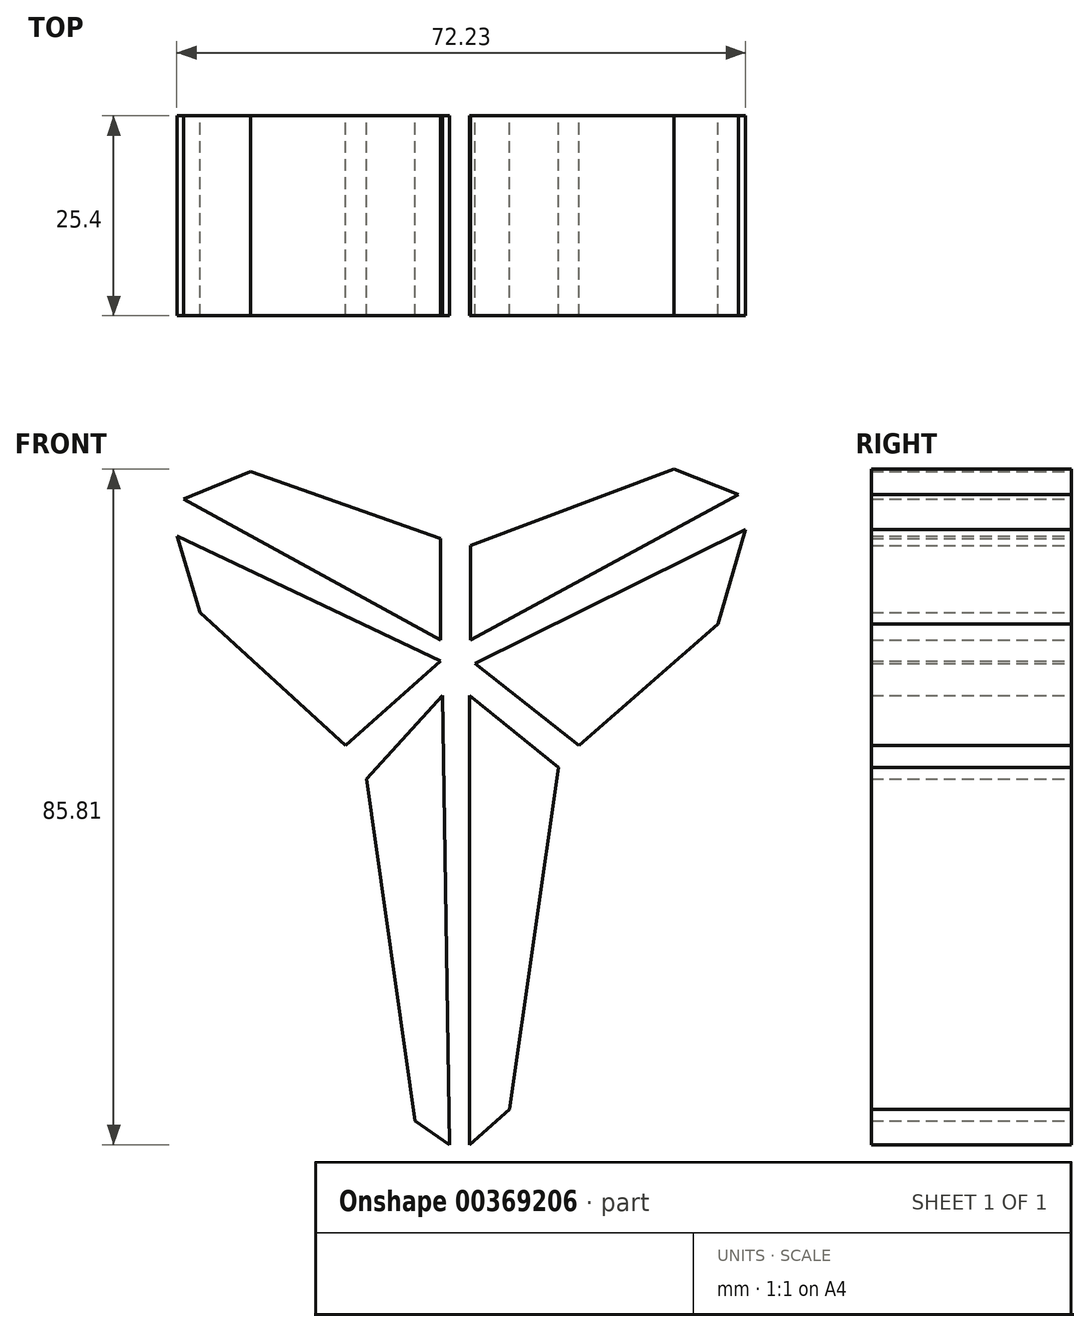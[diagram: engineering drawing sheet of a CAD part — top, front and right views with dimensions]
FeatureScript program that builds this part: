
annotation { "Feature Type Name" : "Feature", "Feature Type Description" : "" }
export const myFeature = defineFeature(function(context is Context, id is Id, definition is map)
    precondition{}
    {
        {
            var Q0;
            Q0=qCreatedBy(makeId("Front.planeOp"),FACE);
            var sketch = newSketch(context, id + "F0", { "sketchPlane" : qUnion([Q0])});
            skLineSegment(sketch, "E0", {"start": v(-23.2, 31.27) * mm, "end": v(-14.68, 34.8) * mm});
            skLineSegment(sketch, "E1", {"start": v(-14.68, 34.8) * mm, "end": v(9.4, 26.28) * mm});
            skLineSegment(sketch, "E2", {"start": v(9.4, 26.28) * mm, "end": v(9.4, 13.36) * mm});
            skLineSegment(sketch, "E3", {"start": v(9.4, 13.36) * mm, "end": v(-23.2, 31.27) * mm});
            skLineSegment(sketch, "E4", {"start": v(13.21, 25.4) * mm, "end": v(13.21, 13.36) * mm});
            skLineSegment(sketch, "E5", {"start": v(13.21, 13.36) * mm, "end": v(47.27, 31.86) * mm});
            skLineSegment(sketch, "E6", {"start": v(47.27, 31.86) * mm, "end": v(39.05, 35.09) * mm});
            skLineSegment(sketch, "E7", {"start": v(39.05, 35.09) * mm, "end": v(13.21, 25.4) * mm});
            skLineSegment(sketch, "E8", {"start": v(-24.08, 26.57) * mm, "end": v(9.4, 10.72) * mm});
            skLineSegment(sketch, "E9", {"start": v(9.4, 10.72) * mm, "end": v(-2.64, 0) * mm});
            skLineSegment(sketch, "E10", {"start": v(-2.64, 0) * mm, "end": v(-21.14, 16.88) * mm});
            skLineSegment(sketch, "E11", {"start": v(-21.14, 16.88) * mm, "end": v(-24.08, 26.57) * mm});
            skLineSegment(sketch, "E12", {"start": v(48.15, 27.45) * mm, "end": v(44.63, 15.41) * mm});
            skLineSegment(sketch, "E13", {"start": v(44.63, 15.41) * mm, "end": v(27.01, 0) * mm});
            skLineSegment(sketch, "E14", {"start": v(27.01, 0) * mm, "end": v(13.8, 10.42) * mm});
            skLineSegment(sketch, "E15", {"start": v(13.8, 10.42) * mm, "end": v(48.15, 27.45) * mm});
            skLineSegment(sketch, "E16", {"start": v(24.37, -2.79) * mm, "end": v(18.2, -46.24) * mm});
            skLineSegment(sketch, "E17", {"start": v(18.2, -46.24) * mm, "end": v(13.1, -50.72) * mm});
            skLineSegment(sketch, "E18", {"start": v(13.1, -50.72) * mm, "end": v(13.1, 6.31) * mm});
            skLineSegment(sketch, "E19", {"start": v(13.1, 6.31) * mm, "end": v(24.37, -2.79) * mm});
            skLineSegment(sketch, "E20", {"start": v(9.69, 6.31) * mm, "end": v(0, -4.26) * mm});
            skPoint(sketch, "E21.endSnap0", {"position": v(-136.2, -23.4) * mm});
            skLineSegment(sketch, "E22", {"start": v(10.57, -50.72) * mm, "end": v(9.69, 6.31) * mm});
            skPoint(sketch, "E23.endSnap0", {"position": v(4.84, 1.03) * mm});
            skLineSegment(sketch, "E24", {"start": v(0, -4.26) * mm, "end": v(6.17, -47.71) * mm});
            skLineSegment(sketch, "E25", {"start": v(6.17, -47.71) * mm, "end": v(10.57, -50.72) * mm});
            skSolve(sketch);
        }
        {
            var Q0;
            Q0 = qSketchRegion(id + "F0", true);
            extrude(context, id + "F1", {"entities" : qUnion([Q0]), "depth" : 25.4 * mm});
        }
    });
